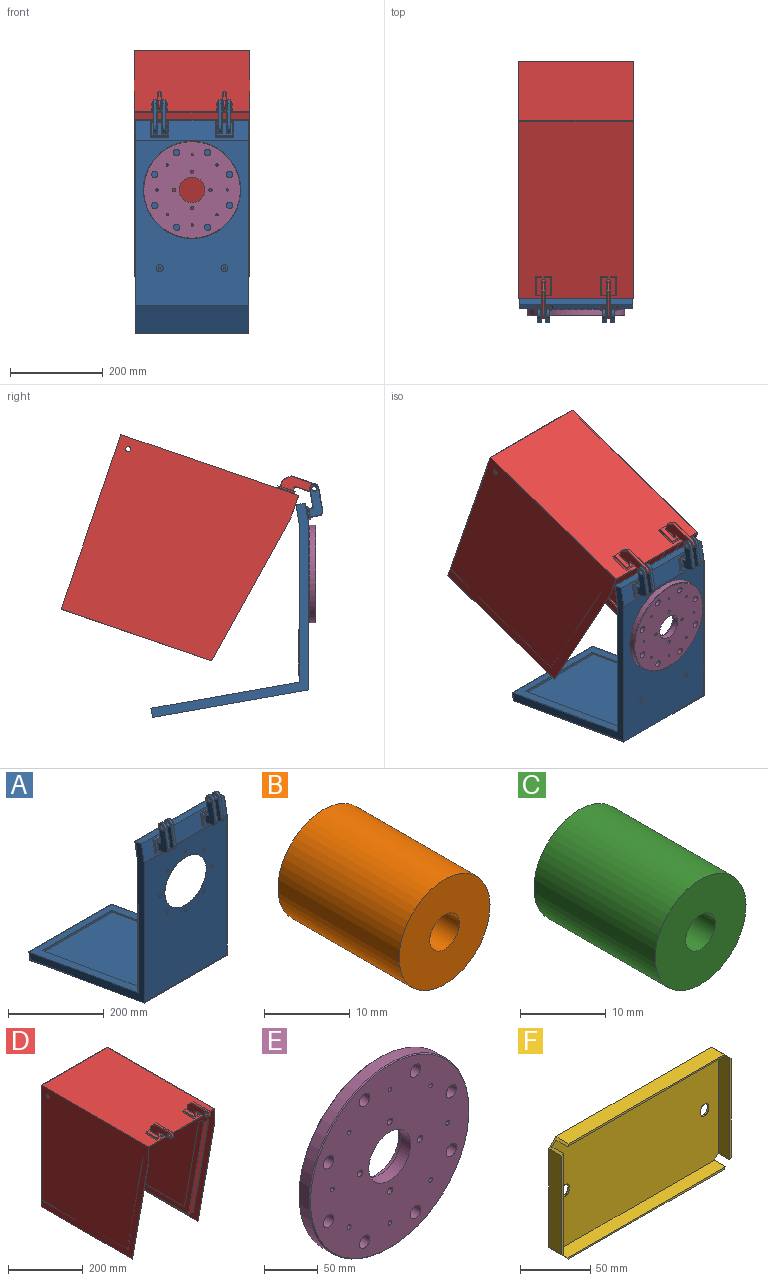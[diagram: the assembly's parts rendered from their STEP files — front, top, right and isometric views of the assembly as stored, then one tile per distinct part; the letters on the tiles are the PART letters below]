
ASSEMBLY  parts=6 mates=5
PART A: 190 faces, bbox 245x370.8x503.5 mm
  f0: plane 36x29.54mm, normal (0,-0.98,0.17), area 656mm2, adj f3,f65,f66,f67,f146,f149,f150,f153
  f1: plane 18.71x6mm, normal (0,-0.17,-0.98), area 114mm2, adj f10,f171,f172,f173
  f2: plane 18.71x6mm, normal (0,-0.17,-0.98), area 114mm2, adj f11,f144,f148,f149
  f3: plane 30.07x8.16mm, normal (1,0,0), area 90mm2, adj f0,f65,f66,f69
  f4: plane 36.44x6.43mm, normal (0,0.98,-0.17), area 222mm2, adj f6,f14,f170,f174
  f5: plane 36.44x6.43mm, normal (0,0.98,-0.17), area 222mm2, adj f7,f15,f145,f160
  f6: cylinder r=10mm len=19.85mm, axis (1,0,0), area 188.5mm2, adj f4,f8,f166,f169
  f7: cylinder r=10mm len=19.85mm, axis (1,0,0), area 188.5mm2, adj f5,f9,f143,f158
  f8: plane 49.24x8.68mm, normal (0,-0.98,0.17), area 300mm2, adj f6,f10,f164,f165
  f9: plane 49.24x8.68mm, normal (0,-0.98,0.17), area 300mm2, adj f7,f11,f141,f155
  f10: cylinder r=10mm len=11.58mm, axis (1,0,0), area 94.2mm2, adj f1,f8,f167,f168
  f11: cylinder r=10mm len=11.58mm, axis (1,0,0), area 94.2mm2, adj f2,f9,f142,f152
  f12: plane 6x5.91mm, normal (0,0.17,0.98), area 36mm2, adj f14,f179,f182,f185
  f13: plane 6x5.91mm, normal (0,0.17,0.98), area 36mm2, adj f15,f151,f157,f161
  f14: cylinder r=3mm len=6mm, axis (1,0,0), area 28.3mm2, adj f4,f12,f175,f178
  f15: cylinder r=3mm len=6mm, axis (1,0,0), area 28.3mm2, adj f5,f13,f147,f162
  f16: cylinder r=5mm len=10mm, axis (1,0,0), area 188.5mm2, adj f186,f187
  f17: plane 36x29.54mm, normal (0,-0.98,0.17), area 656mm2, adj f61,f62,f63,f64,f94,f98,f99,f102
  f18: plane 18.71x6mm, normal (0,-0.17,-0.98), area 114mm2, adj f82,f113,f118,f119
  f19: plane 49.24x8.68mm, normal (0,-0.98,0.17), area 300mm2, adj f20,f24,f88,f96
  f20: cylinder r=10mm len=19.85mm, axis (1,0,0), area 188.5mm2, adj f19,f21,f90,f101
  f21: plane 36.44x6.43mm, normal (0,0.98,-0.17), area 222mm2, adj f20,f22,f92,f104
  f22: cylinder r=3mm len=6mm, axis (1,0,0), area 28.3mm2, adj f21,f23,f95,f107
  f23: plane 6x5.91mm, normal (0,0.17,0.98), area 36mm2, adj f22,f100,f106,f109
  f24: cylinder r=10mm len=11.58mm, axis (1,0,0), area 94.2mm2, adj f19,f81,f89,f93
  f25: cylinder r=5mm len=10mm, axis (1,0,0), area 188.5mm2, adj f132,f134
  f26: plane 245x45.3mm, normal (0,-0.98,0.17), area 8550mm2, adj f34,f38,f39,f40,f68,f69,f70,f71
  f27: plane 339.86x18.5mm, normal (0,-1,0), area 6287.4mm2, adj f29,f45,f56,f57
  f28: plane 245x43.58mm, normal (0,0.98,-0.17), area 5870mm2, adj f30,f37,f38,f39,f40,f57,f59,f60
  f29: plane 320.04x242mm, normal (0,-0.17,-0.98), area 15816.6mm2, adj f27,f31,f44,f45,f46,f57,f58,f59
  f30: plane 338.47x20mm, normal (0,1,0), area 6769.4mm2, adj f28,f33,f40,f59
  f31: plane 339.86x18.5mm, normal (0,-1,0), area 6287.4mm2, adj f29,f46,f56,f59
  f32: plane 242x16.74mm, normal (0,-0.17,-0.98), area 4114mm2, adj f41,f45,f46,f56
  f33: plane 320.28x245mm, normal (0,0.17,0.98), area 17108.7mm2, adj f30,f36,f37,f39,f40,f57,f58,f59
  f34: plane 357x245mm, normal (0,-1,0), area 75428.9mm2, adj f26,f35,f39,f40,f47,f48,f49,f50
  f35: plane 336.8x245mm, normal (0,-0.17,-0.98), area 83790mm2, adj f34,f36,f39,f40
  f36: plane 245x19.7mm, normal (0,0.98,-0.17), area 4900mm2, adj f33,f35,f39,f40
  f37: plane 338.47x20mm, normal (0,1,0), area 6769.4mm2, adj f28,f33,f39,f57
  f38: plane 245x19.7mm, normal (0,0.17,0.98), area 4900mm2, adj f26,f28,f39,f40
  f39: plane 461.69x340.28mm, normal (1,0,0), area 14529.4mm2, adj f26,f28,f33,f34,f35,f36,f37,f38
  f40: plane 461.69x340.28mm, normal (-1,0,0), area 14529.4mm2, adj f26,f28,f30,f33,f34,f35,f36,f38
  f41: plane 242x43.69mm, normal (0,0.98,-0.17), area 10737.2mm2, adj f32,f42,f45,f46
  f42: plane 355.61x242mm, normal (0,1,0), area 73634.5mm2, adj f41,f43,f45,f46,f47,f48,f49,f50
  f43: plane 334.09x242mm, normal (0,0.17,0.98), area 82096.4mm2, adj f42,f44,f45,f46
  f44: plane 242x16.74mm, normal (0,-0.98,0.17), area 4114mm2, adj f29,f43,f45,f46
  f45: plane 458.21x337.04mm, normal (-1,0,0), area 12299mm2, adj f27,f29,f32,f41,f42,f43,f44,f56
  f46: plane 458.21x337.04mm, normal (1,0,0), area 12299mm2, adj f29,f31,f32,f41,f42,f43,f44,f56
  f47: cylinder r=3.5mm len=7mm, axis (0,-1,0), area 33mm2, adj f34,f42
  f48: cylinder r=3.5mm len=7mm, axis (0,-1,0), area 33mm2, adj f34,f42
  f49: cylinder r=3.5mm len=7mm, axis (0,-1,0), area 33mm2, adj f34,f42
  f50: cylinder r=3.5mm len=7mm, axis (0,-1,0), area 33mm2, adj f34,f42
  f51: cylinder r=3.5mm len=7mm, axis (0,-1,0), area 33mm2, adj f34,f42
  f52: cylinder r=61.1mm len=122.2mm, axis (0,-1,0), area 192mm2, adj f34,f189
  f53: cylinder r=3.5mm len=7mm, axis (0,-1,0), area 33mm2, adj f34,f42
  f54: cylinder r=3.5mm len=7mm, axis (0,-1,0), area 33mm2, adj f34,f42
  f55: cylinder r=3.5mm len=7mm, axis (0,-1,0), area 33mm2, adj f34,f42
  f56: plane 242x42.23mm, normal (0,-0.98,0.17), area 5379.1mm2, adj f27,f31,f32,f45,f46,f57,f59,f60
  f57: plane 417.09x302.08mm, normal (-1,0,0), area 1004mm2, adj f27,f28,f29,f33,f37,f56,f58,f60
  f58: plane 205x1.48mm, normal (0,-0.98,0.17), area 307.5mm2, adj f29,f33,f57,f59
  f59: plane 417.09x302.08mm, normal (1,0,0), area 1004mm2, adj f28,f29,f30,f31,f33,f56,f58,f60
  f60: plane 205x1.48mm, normal (0,-0.17,-0.98), area 307.5mm2, adj f28,f56,f57,f59
  f61: plane 30.07x8.16mm, normal (-1,0,0), area 90mm2, adj f17,f62,f64,f72
  f62: plane 36x2.95mm, normal (0,-0.17,-0.98), area 108mm2, adj f17,f61,f63,f74
  f63: plane 30.07x8.16mm, normal (1,0,0), area 90mm2, adj f17,f62,f64,f75
  f64: plane 36x2.95mm, normal (0,0.17,0.98), area 108mm2, adj f17,f61,f63,f73
  f65: plane 36x2.95mm, normal (0,-0.17,-0.98), area 108mm2, adj f0,f3,f67,f68
  f66: plane 36x2.95mm, normal (0,0.17,0.98), area 108mm2, adj f0,f3,f67,f71
  f67: plane 30.07x8.16mm, normal (-1,0,0), area 90mm2, adj f0,f65,f66,f70
  f68: plane 40x2.32mm, normal (0,-0.82,-0.57), area 107.5mm2, adj f26,f65,f69,f70
  f69: plane 33.48x7.53mm, normal (0.71,-0.7,0.12), area 90.5mm2, adj f3,f26,f68,f71
  f70: plane 33.48x7.53mm, normal (-0.71,-0.7,0.12), area 90.5mm2, adj f26,f67,f68,f71
  f71: plane 40x2.32mm, normal (0,-0.57,0.82), area 107.5mm2, adj f26,f66,f69,f70
  f72: plane 33.48x7.53mm, normal (-0.71,-0.7,0.12), area 90.5mm2, adj f26,f61,f73,f74
  f73: plane 40x2.32mm, normal (0,-0.57,0.82), area 107.5mm2, adj f26,f64,f72,f75
  f74: plane 40x2.32mm, normal (0,-0.82,-0.57), area 107.5mm2, adj f26,f62,f72,f75
  f75: plane 33.48x7.53mm, normal (0.71,-0.7,0.12), area 90.5mm2, adj f26,f63,f73,f74
  f76: plane 49.24x8.68mm, normal (0,-0.98,0.17), area 300mm2, adj f77,f82,f110,f122
  f77: cylinder r=10mm len=19.85mm, axis (1,0,0), area 188.5mm2, adj f76,f78,f112,f125
  f78: plane 36.44x6.43mm, normal (0,0.98,-0.17), area 222mm2, adj f77,f79,f114,f128
  f79: cylinder r=3mm len=6mm, axis (1,0,0), area 28.3mm2, adj f78,f80,f116,f130
  f80: plane 6x5.91mm, normal (0,0.17,0.98), area 36mm2, adj f79,f121,f127,f131
  f81: plane 18.71x6mm, normal (0,-0.17,-0.98), area 114mm2, adj f24,f91,f97,f98
  f82: cylinder r=10mm len=11.58mm, axis (1,0,0), area 94.2mm2, adj f18,f76,f111,f117
  f83: cylinder r=5mm len=10mm, axis (1,0,0), area 188.5mm2, adj f133,f135
  f84: plane 70.4x29.27mm, normal (-1,0,0), area 1242.2mm2, adj f93,f96,f97,f101,f104,f105,f107,f109
  f85: plane 70.4x29.27mm, normal (1,0,0), area 1242.2mm2, adj f110,f111,f112,f113,f114,f116,f120,f121
  f86: plane 70.4x29.27mm, normal (1,0,0), area 1242.2mm2, adj f88,f89,f90,f91,f92,f95,f99,f100
  f87: plane 70.4x29.27mm, normal (-1,0,0), area 1242.2mm2, adj f117,f118,f122,f125,f126,f128,f130,f131
  f88: plane 49.41x9.67mm, normal (0.71,-0.7,0.12), area 70.7mm2, adj f19,f86,f89,f90
  f89: cone r=9mm half-angle=45deg, axis (-1,0,0), area 21.1mm2, adj f24,f86,f88,f91
  f90: cone r=9mm half-angle=45deg, axis (-1,0,0), area 42.2mm2, adj f20,f86,f88,f92
  f91: plane 18.89x4.28mm, normal (0.71,-0.12,-0.7), area 26.9mm2, adj f81,f86,f89,f94
  f92: plane 36.61x7.41mm, normal (0.71,0.7,-0.12), area 52.3mm2, adj f21,f86,f90,f95
  f93: cone r=9mm half-angle=45deg, axis (1,0,0), area 21.1mm2, adj f24,f84,f96,f97
  f94: plane 2.14x2mm, normal (0.58,-0.67,-0.47), area 2.6mm2, adj f17,f91,f98,f99
  f95: cone r=3mm half-angle=45deg, axis (1,0,0), area 7.8mm2, adj f22,f86,f92,f100
  f96: plane 49.41x9.67mm, normal (-0.71,-0.7,0.12), area 70.7mm2, adj f19,f84,f93,f101
  f97: plane 18.89x4.28mm, normal (-0.71,-0.12,-0.7), area 26.9mm2, adj f81,f84,f93,f102
  f98: plane 6x1.16mm, normal (0,-0.82,-0.57), area 8.5mm2, adj f17,f81,f94,f102
  f99: plane 17.9x4.11mm, normal (0.71,-0.7,0.12), area 25.5mm2, adj f17,f86,f94,f103
  f100: plane 6.08x2.03mm, normal (0.71,0.12,0.7), area 8.5mm2, adj f23,f86,f95,f103
  f101: cone r=9mm half-angle=45deg, axis (1,0,0), area 42.2mm2, adj f20,f84,f96,f104
  f102: plane 2.14x2mm, normal (-0.58,-0.67,-0.47), area 2.6mm2, adj f17,f97,f98,f105
  f103: plane 2x1.97mm, normal (0.58,-0.47,0.67), area 2.6mm2, adj f17,f99,f100,f106
  f104: plane 36.61x7.41mm, normal (-0.71,0.7,-0.12), area 52.3mm2, adj f21,f84,f101,f107
  f105: plane 17.9x4.11mm, normal (-0.71,-0.7,0.12), area 25.5mm2, adj f17,f84,f102,f108
  f106: plane 6x1.16mm, normal (0,-0.57,0.82), area 8.5mm2, adj f17,f23,f103,f108
  f107: cone r=3mm half-angle=45deg, axis (-1,0,0), area 7.8mm2, adj f22,f84,f104,f109
  f108: plane 2x1.97mm, normal (-0.58,-0.47,0.67), area 2.6mm2, adj f17,f105,f106,f109
  f109: plane 6.08x2.03mm, normal (-0.71,0.12,0.7), area 8.5mm2, adj f23,f84,f107,f108
  f110: plane 49.41x9.67mm, normal (0.71,-0.7,0.12), area 70.7mm2, adj f76,f85,f111,f112
  f111: cone r=10mm half-angle=45deg, axis (-1,0,0), area 21.1mm2, adj f82,f85,f110,f113
  f112: cone r=10mm half-angle=45deg, axis (-1,0,0), area 42.2mm2, adj f77,f85,f110,f114
  f113: plane 18.89x4.28mm, normal (0.71,-0.12,-0.7), area 26.9mm2, adj f18,f85,f111,f115
  f114: plane 36.61x7.41mm, normal (0.71,0.7,-0.12), area 52.3mm2, adj f78,f85,f112,f116
  f115: plane 2.14x2mm, normal (0.58,-0.67,-0.47), area 2.6mm2, adj f17,f113,f119,f120
  f116: cone r=4mm half-angle=45deg, axis (1,0,0), area 7.8mm2, adj f79,f85,f114,f121
  f117: cone r=10mm half-angle=45deg, axis (1,0,0), area 21.1mm2, adj f82,f87,f118,f122
  f118: plane 18.89x4.28mm, normal (-0.71,-0.12,-0.7), area 26.9mm2, adj f18,f87,f117,f123
  f119: plane 6x1.16mm, normal (0,-0.82,-0.57), area 8.5mm2, adj f17,f18,f115,f123
  f120: plane 17.9x4.11mm, normal (0.71,-0.7,0.12), area 25.5mm2, adj f17,f85,f115,f124
  f121: plane 6.08x2.03mm, normal (0.71,0.12,0.7), area 8.5mm2, adj f80,f85,f116,f124
  f122: plane 49.41x9.67mm, normal (-0.71,-0.7,0.12), area 70.7mm2, adj f76,f87,f117,f125
  f123: plane 2.14x2mm, normal (-0.58,-0.67,-0.47), area 2.6mm2, adj f17,f118,f119,f126
  f124: plane 2x1.97mm, normal (0.58,-0.47,0.67), area 2.6mm2, adj f17,f120,f121,f127
  f125: cone r=10mm half-angle=45deg, axis (1,0,0), area 42.2mm2, adj f77,f87,f122,f128
  f126: plane 17.9x4.11mm, normal (-0.71,-0.7,0.12), area 25.5mm2, adj f17,f87,f123,f129
  f127: plane 6x1.16mm, normal (0,-0.57,0.82), area 8.5mm2, adj f17,f80,f124,f129
  f128: plane 36.61x7.41mm, normal (-0.71,0.7,-0.12), area 52.3mm2, adj f78,f87,f125,f130
  f129: plane 2x1.97mm, normal (-0.58,-0.47,0.67), area 2.6mm2, adj f17,f126,f127,f131
  f130: cone r=4mm half-angle=45deg, axis (-1,0,0), area 7.8mm2, adj f79,f87,f128,f131
  f131: plane 6.08x2.03mm, normal (-0.71,0.12,0.7), area 8.5mm2, adj f80,f87,f129,f130
  f132: cone r=5mm half-angle=45deg, axis (-1,0,0), area 48.9mm2, adj f25,f84
  f133: cone r=6mm half-angle=45deg, axis (-1,0,0), area 48.9mm2, adj f83,f87
  f134: cone r=5mm half-angle=45deg, axis (1,0,0), area 48.9mm2, adj f25,f86
  f135: cone r=6mm half-angle=45deg, axis (1,0,0), area 48.9mm2, adj f83,f85
  f136: plane 70.4x29.27mm, normal (-1,0,0), area 1242.2mm2, adj f164,f166,f167,f170,f171,f175,f179,f180
  f137: plane 70.4x29.27mm, normal (1,0,0), area 1242.2mm2, adj f141,f142,f143,f144,f145,f147,f150,f151
  f138: plane 70.4x29.27mm, normal (1,0,0), area 1242.2mm2, adj f165,f168,f169,f173,f174,f178,f181,f182
  f139: plane 70.4x29.27mm, normal (-1,0,0), area 1242.2mm2, adj f148,f152,f155,f156,f158,f160,f161,f162
  f140: cylinder r=5mm len=10mm, axis (1,0,0), area 188.5mm2, adj f163,f188
  f141: plane 49.41x9.67mm, normal (0.71,-0.7,0.12), area 70.7mm2, adj f9,f137,f142,f143
  f142: cone r=10mm half-angle=45deg, axis (-1,0,0), area 21.1mm2, adj f11,f137,f141,f144
  f143: cone r=10mm half-angle=45deg, axis (-1,0,0), area 42.2mm2, adj f7,f137,f141,f145
  f144: plane 18.89x4.28mm, normal (0.71,-0.12,-0.7), area 26.9mm2, adj f2,f137,f142,f146
  f145: plane 36.61x7.41mm, normal (0.71,0.7,-0.12), area 52.3mm2, adj f5,f137,f143,f147
  f146: plane 2.14x2mm, normal (0.58,-0.67,-0.47), area 2.6mm2, adj f0,f144,f149,f150
  f147: cone r=4mm half-angle=45deg, axis (1,0,0), area 7.8mm2, adj f15,f137,f145,f151
  f148: plane 18.89x4.28mm, normal (-0.71,-0.12,-0.7), area 26.9mm2, adj f2,f139,f152,f153
  f149: plane 6x1.16mm, normal (0,-0.82,-0.57), area 8.5mm2, adj f0,f2,f146,f153
  f150: plane 17.9x4.11mm, normal (0.71,-0.7,0.12), area 25.5mm2, adj f0,f137,f146,f154
  f151: plane 6.08x2.03mm, normal (0.71,0.12,0.7), area 8.5mm2, adj f13,f137,f147,f154
  f152: cone r=10mm half-angle=45deg, axis (1,0,0), area 21.1mm2, adj f11,f139,f148,f155
  f153: plane 2.14x2mm, normal (-0.58,-0.67,-0.47), area 2.6mm2, adj f0,f148,f149,f156
  f154: plane 2x1.97mm, normal (0.58,-0.47,0.67), area 2.6mm2, adj f0,f150,f151,f157
  f155: plane 49.41x9.67mm, normal (-0.71,-0.7,0.12), area 70.7mm2, adj f9,f139,f152,f158
  f156: plane 17.9x4.11mm, normal (-0.71,-0.7,0.12), area 25.5mm2, adj f0,f139,f153,f159
  f157: plane 6x1.16mm, normal (0,-0.57,0.82), area 8.5mm2, adj f0,f13,f154,f159
  f158: cone r=10mm half-angle=45deg, axis (1,0,0), area 42.2mm2, adj f7,f139,f155,f160
  f159: plane 2x1.97mm, normal (-0.58,-0.47,0.67), area 2.6mm2, adj f0,f156,f157,f161
  f160: plane 36.61x7.41mm, normal (-0.71,0.7,-0.12), area 52.3mm2, adj f5,f139,f158,f162
  f161: plane 6.08x2.03mm, normal (-0.71,0.12,0.7), area 8.5mm2, adj f13,f139,f159,f162
  f162: cone r=4mm half-angle=45deg, axis (-1,0,0), area 7.8mm2, adj f15,f139,f160,f161
  f163: cone r=6mm half-angle=45deg, axis (-1,0,0), area 48.9mm2, adj f139,f140
  f164: plane 49.41x9.67mm, normal (-0.71,-0.7,0.12), area 70.7mm2, adj f8,f136,f166,f167
  f165: plane 49.41x9.67mm, normal (0.71,-0.7,0.12), area 70.7mm2, adj f8,f138,f168,f169
  f166: cone r=10mm half-angle=45deg, axis (1,0,0), area 42.2mm2, adj f6,f136,f164,f170
  f167: cone r=10mm half-angle=45deg, axis (1,0,0), area 21.1mm2, adj f10,f136,f164,f171
  f168: cone r=10mm half-angle=45deg, axis (-1,0,0), area 21.1mm2, adj f10,f138,f165,f173
  f169: cone r=10mm half-angle=45deg, axis (-1,0,0), area 42.2mm2, adj f6,f138,f165,f174
  f170: plane 36.61x7.41mm, normal (-0.71,0.7,-0.12), area 52.3mm2, adj f4,f136,f166,f175
  f171: plane 18.89x4.28mm, normal (-0.71,-0.12,-0.7), area 26.9mm2, adj f1,f136,f167,f176
  f172: plane 6x1.16mm, normal (0,-0.82,-0.57), area 8.5mm2, adj f0,f1,f176,f177
  f173: plane 18.89x4.28mm, normal (0.71,-0.12,-0.7), area 26.9mm2, adj f1,f138,f168,f177
  f174: plane 36.61x7.41mm, normal (0.71,0.7,-0.12), area 52.3mm2, adj f4,f138,f169,f178
  f175: cone r=4mm half-angle=45deg, axis (-1,0,0), area 7.8mm2, adj f14,f136,f170,f179
  f176: plane 2.14x2mm, normal (-0.58,-0.67,-0.47), area 2.6mm2, adj f0,f171,f172,f180
  f177: plane 2.14x2mm, normal (0.58,-0.67,-0.47), area 2.6mm2, adj f0,f172,f173,f181
  f178: cone r=4mm half-angle=45deg, axis (1,0,0), area 7.8mm2, adj f14,f138,f174,f182
  f179: plane 6.08x2.03mm, normal (-0.71,0.12,0.7), area 8.5mm2, adj f12,f136,f175,f183
  f180: plane 17.9x4.11mm, normal (-0.71,-0.7,0.12), area 25.5mm2, adj f0,f136,f176,f183
  f181: plane 17.9x4.11mm, normal (0.71,-0.7,0.12), area 25.5mm2, adj f0,f138,f177,f184
  f182: plane 6.08x2.03mm, normal (0.71,0.12,0.7), area 8.5mm2, adj f12,f138,f178,f184
  f183: plane 2x1.97mm, normal (-0.58,-0.47,0.67), area 2.6mm2, adj f0,f179,f180,f185
  f184: plane 2x1.97mm, normal (0.58,-0.47,0.67), area 2.6mm2, adj f0,f181,f182,f185
  f185: plane 6x1.16mm, normal (0,-0.57,0.82), area 8.5mm2, adj f0,f12,f183,f184
  f186: cone r=6mm half-angle=45deg, axis (-1,0,0), area 48.9mm2, adj f16,f136
  f187: cone r=6mm half-angle=45deg, axis (1,0,0), area 48.9mm2, adj f16,f138
  f188: cone r=6mm half-angle=45deg, axis (1,0,0), area 48.9mm2, adj f137,f140
  f189: cone r=61.1mm half-angle=45deg, axis (0,1,0), area 547.4mm2, adj f42,f52
PART B: 4 faces, bbox 15x20x15 mm
  f0: cylinder r=2.46mm len=20mm, axis (0,1,0), area 309.1mm2, adj f2,f3
  f1: cylinder r=7.5mm len=20mm, axis (0,1,0), area 942.5mm2, adj f2,f3
  f2: plane 15x15mm, normal (0,-1,0), area 157.7mm2, adj f0,f1
  f3: plane 15x15mm, normal (0,1,0), area 157.7mm2, adj f0,f1
PART C: 4 faces, bbox 15x20x15 mm
  f0: cylinder r=7.5mm len=20mm, axis (0,1,0), area 942.5mm2, adj f2,f3
  f1: cylinder r=2.46mm len=20mm, axis (0,1,0), area 309.1mm2, adj f2,f3
  f2: plane 15x15mm, normal (0,-1,0), area 157.7mm2, adj f0,f1
  f3: plane 15x15mm, normal (0,1,0), area 157.7mm2, adj f0,f1
PART D: 128 faces, bbox 250x442x433 mm
  f0: plane 40x30mm, normal (0,0,1), area 888mm2, adj f68,f69,f70,f71,f104,f105,f108,f109
  f1: plane 40x30mm, normal (0,0,1), area 888mm2, adj f64,f65,f66,f67,f82,f83,f86,f87
  f2: plane 38x6mm, normal (0,0,-1), area 228mm2, adj f3,f8,f94,f95
  f3: cylinder r=10mm len=20mm, axis (-1,0,0), area 188.5mm2, adj f2,f4,f97,f98
  f4: plane 56x6mm, normal (0,0,1), area 336mm2, adj f3,f5,f101,f102
  f5: plane 15x15mm, normal (0,0.71,0.71), area 127.3mm2, adj f4,f6,f106,f107
  f6: plane 14x6mm, normal (0,1,0), area 84mm2, adj f5,f110,f111,f115
  f7: plane 6x6mm, normal (0,-1,0), area 36mm2, adj f8,f100,f103,f104
  f8: cylinder r=3mm len=6mm, axis (-1,0,0), area 28.3mm2, adj f2,f7,f96,f99
  f9: cylinder r=5mm len=10mm, axis (-1,0,0), area 188.5mm2, adj f117,f119
  f10: plane 79x28mm, normal (1,0,0), area 1453.7mm2, adj f94,f96,f97,f100,f101,f106,f109,f110
  f11: plane 79x28mm, normal (-1,0,0), area 1453.7mm2, adj f95,f98,f99,f102,f103,f107,f111,f112
  f12: plane 38x6mm, normal (0,0,-1), area 228mm2, adj f13,f18,f72,f73
  f13: cylinder r=10mm len=20mm, axis (-1,0,0), area 188.5mm2, adj f12,f14,f75,f76
  f14: plane 56x6mm, normal (0,0,1), area 336mm2, adj f13,f15,f79,f80
  f15: plane 15x15mm, normal (0,0.71,0.71), area 127.3mm2, adj f14,f16,f84,f85
  f16: plane 14x6mm, normal (0,1,0), area 84mm2, adj f15,f88,f89,f93
  f17: plane 6x6mm, normal (0,-1,0), area 36mm2, adj f18,f78,f81,f82
  f18: cylinder r=3mm len=6mm, axis (-1,0,0), area 28.3mm2, adj f12,f17,f74,f77
  f19: cylinder r=5mm len=10mm, axis (-1,0,0), area 188.5mm2, adj f116,f118
  f20: plane 79x28mm, normal (1,0,0), area 1453.7mm2, adj f72,f74,f75,f78,f79,f84,f87,f88
  f21: plane 79x28mm, normal (-1,0,0), area 1453.7mm2, adj f73,f76,f77,f80,f81,f85,f89,f90
  f22: plane 18x3.94mm, normal (0,-0.17,0.98), area 29.7mm2, adj f34,f51,f57,f58,f60,f61,f62
  f23: plane 343.5x250mm, normal (0,0,-1), area 1401mm2, adj f24,f27,f28,f29,f30,f32,f33,f34
  f24: plane 348.78x61.5mm, normal (0,-0.98,-0.17), area 531.2mm2, adj f23,f25,f30,f34
  f25: plane 250x49.22mm, normal (0,-1,0), area 518.1mm2, adj f24,f26,f27,f29,f30,f31,f33,f34
  f26: plane 405x250mm, normal (0,0,1), area 98258mm2, adj f25,f28,f29,f30,f120,f121,f122,f123
  f27: plane 348.78x61.5mm, normal (0,-0.98,-0.17), area 531.2mm2, adj f23,f25,f29,f33
  f28: plane 398x250mm, normal (0,1,0), area 99500mm2, adj f23,f26,f29,f30
  f29: plane 405x398mm, normal (1,0,0), area 150369.9mm2, adj f23,f25,f26,f27,f28,f36
  f30: plane 405x398mm, normal (-1,0,0), area 150369.9mm2, adj f23,f24,f25,f26,f28,f35
  f31: plane 403.5x247mm, normal (0,0,-1), area 99664.5mm2, adj f25,f32,f33,f34
  f32: plane 396.5x247mm, normal (0,-1,0), area 97935.5mm2, adj f23,f31,f33,f34
  f33: plane 403.5x396.5mm, normal (-1,0,0), area 147520.5mm2, adj f23,f25,f27,f31,f32,f36,f39,f44
  f34: plane 403.5x396.5mm, normal (1,0,0), area 147521.2mm2, adj f22,f23,f24,f25,f31,f32,f35,f55
  f35: cylinder r=5.5mm len=11mm, axis (1,0,0), area 51.8mm2, adj f30,f34
  f36: cylinder r=5.5mm len=11mm, axis (1,0,0), area 51.8mm2, adj f29,f33
  f37: plane 331.88x58.52mm, normal (0,-0.98,-0.17), area 5729mm2, adj f38,f44,f45,f49
  f38: plane 322.27x17mm, normal (0,0,-1), area 5478.7mm2, adj f37,f39,f45,f50
  f39: plane 18x4mm, normal (0,1,0), area 29.8mm2, adj f33,f38,f40,f45,f47,f48,f50
  f40: cylinder r=15mm len=15mm, axis (1,0,0), area 35.3mm2, adj f39,f41,f45,f48
  f41: plane 292.17x1.5mm, normal (0,0,1), area 438.3mm2, adj f40,f42,f45,f48
  f42: plane 302.23x53.29mm, normal (0,0.98,0.17), area 460.3mm2, adj f41,f43,f45,f48
  f43: cylinder r=15mm len=17.38mm, axis (1,0,0), area 35.3mm2, adj f42,f44,f45,f48
  f44: plane 18x3.94mm, normal (0,-0.17,0.98), area 29.7mm2, adj f33,f37,f43,f45,f46,f48,f49
  f45: plane 380.79x332.63mm, normal (-1,0,0), area 11498.5mm2, adj f37,f38,f39,f40,f41,f42,f43,f44
  f46: plane 330.64x58.3mm, normal (0,0.98,0.17), area 5539.7mm2, adj f33,f44,f47,f48
  f47: plane 321.02x16.5mm, normal (0,0,1), area 5296.8mm2, adj f33,f39,f46,f48
  f48: plane 379.32x331.13mm, normal (1,0,0), area 10511.5mm2, adj f39,f40,f41,f42,f43,f44,f46,f47
  f49: plane 332.88x59.5mm, normal (-0.71,-0.7,-0.12), area 477.2mm2, adj f33,f37,f44,f50
  f50: plane 323.11x1mm, normal (-0.71,0,-0.71), area 456.4mm2, adj f33,f38,f39,f49
  f51: cylinder r=15mm len=17.38mm, axis (-1,0,0), area 35.3mm2, adj f22,f52,f58,f61
  f52: plane 302.23x53.29mm, normal (0,0.98,0.17), area 460.3mm2, adj f51,f53,f58,f61
  f53: plane 291.9x1.5mm, normal (0,0,1), area 437.8mm2, adj f52,f54,f58,f61
  f54: cylinder r=15mm len=15mm, axis (-1,0,0), area 35.3mm2, adj f53,f55,f58,f61
  f55: plane 18x4mm, normal (0,1,0), area 29.8mm2, adj f34,f54,f56,f58,f59,f61,f63
  f56: plane 322x17mm, normal (0,0,-1), area 5474mm2, adj f55,f57,f58,f63
  f57: plane 331.88x58.52mm, normal (0,-0.98,-0.17), area 5729mm2, adj f22,f56,f58,f62
  f58: plane 380.52x332.63mm, normal (1,0,0), area 11493.6mm2, adj f22,f51,f52,f53,f54,f55,f56,f57
  f59: plane 320.74x16.5mm, normal (0,0,1), area 5292.2mm2, adj f34,f55,f60,f61
  f60: plane 330.64x58.3mm, normal (0,0.98,0.17), area 5539.7mm2, adj f22,f34,f59,f61
  f61: plane 379.04x331.13mm, normal (-1,0,0), area 10506.9mm2, adj f22,f51,f52,f53,f54,f55,f59,f60
  f62: plane 332.88x59.5mm, normal (0.71,-0.7,-0.12), area 477.2mm2, adj f22,f34,f57,f63
  f63: plane 322.84x1mm, normal (0.71,0,-0.71), area 456mm2, adj f34,f55,f56,f62
  f64: plane 40x3mm, normal (1,0,0), area 120mm2, adj f1,f65,f67,f124
  f65: plane 30x3mm, normal (0,1,0), area 90mm2, adj f1,f64,f66,f125
  f66: plane 40x3mm, normal (-1,0,0), area 120mm2, adj f1,f65,f67,f127
  f67: plane 30x3mm, normal (0,-1,0), area 90mm2, adj f1,f64,f66,f126
  f68: plane 40x3mm, normal (1,0,0), area 120mm2, adj f0,f69,f71,f121
  f69: plane 30x3mm, normal (0,1,0), area 90mm2, adj f0,f68,f70,f123
  f70: plane 40x3mm, normal (-1,0,0), area 120mm2, adj f0,f69,f71,f122
  f71: plane 30x3mm, normal (0,-1,0), area 90mm2, adj f0,f68,f70,f120
  f72: plane 38x1mm, normal (0.71,0,-0.71), area 53.7mm2, adj f12,f20,f74,f75
  f73: plane 38x1mm, normal (-0.71,0,-0.71), area 53.7mm2, adj f12,f21,f76,f77
  f74: cone r=4mm half-angle=45deg, axis (1,0,0), area 7.8mm2, adj f18,f20,f72,f78
  f75: cone r=10mm half-angle=45deg, axis (-1,0,0), area 42.2mm2, adj f13,f20,f72,f79
  f76: cone r=9mm half-angle=45deg, axis (1,0,0), area 42.2mm2, adj f13,f21,f73,f80
  f77: cone r=3mm half-angle=45deg, axis (-1,0,0), area 7.8mm2, adj f18,f21,f73,f81
  f78: plane 6x1mm, normal (0.71,-0.71,0), area 8.5mm2, adj f17,f20,f74,f83
  f79: plane 56x1mm, normal (0.71,0,0.71), area 78.9mm2, adj f14,f20,f75,f84
  f80: plane 56x1mm, normal (-0.71,0,0.71), area 78.9mm2, adj f14,f21,f76,f85
  f81: plane 6x1mm, normal (-0.71,-0.71,0), area 8.5mm2, adj f17,f21,f77,f86
  f82: plane 6x1mm, normal (0,-0.71,0.71), area 8.5mm2, adj f1,f17,f83,f86
  f83: plane 2x2mm, normal (0.58,-0.58,0.58), area 2.6mm2, adj f1,f78,f82,f87
  f84: plane 15.41x15.41mm, normal (0.71,0.5,0.5), area 29.4mm2, adj f15,f20,f79,f88
  f85: plane 15.41x15.41mm, normal (-0.71,0.5,0.5), area 29.4mm2, adj f15,f21,f80,f89
  f86: plane 2x2mm, normal (-0.58,-0.58,0.58), area 2.6mm2, adj f1,f81,f82,f90
  f87: plane 28x1mm, normal (0.71,0,0.71), area 39.6mm2, adj f1,f20,f83,f91
  f88: plane 14x1mm, normal (0.71,0.71,0), area 19.5mm2, adj f16,f20,f84,f91
  f89: plane 14x1mm, normal (-0.71,0.71,0), area 19.5mm2, adj f16,f21,f85,f92
  f90: plane 28x1mm, normal (-0.71,0,0.71), area 39.6mm2, adj f1,f21,f86,f92
  f91: plane 2x2mm, normal (0.58,0.58,0.58), area 2.6mm2, adj f1,f87,f88,f93
  f92: plane 2x2mm, normal (-0.58,0.58,0.58), area 2.6mm2, adj f1,f89,f90,f93
  f93: plane 6x1mm, normal (0,0.71,0.71), area 8.5mm2, adj f1,f16,f91,f92
  f94: plane 38x1mm, normal (0.71,0,-0.71), area 53.7mm2, adj f2,f10,f96,f97
  f95: plane 38x1mm, normal (-0.71,0,-0.71), area 53.7mm2, adj f2,f11,f98,f99
  f96: cone r=4mm half-angle=45deg, axis (1,0,0), area 7.8mm2, adj f8,f10,f94,f100
  f97: cone r=10mm half-angle=45deg, axis (-1,0,0), area 42.2mm2, adj f3,f10,f94,f101
  f98: cone r=9mm half-angle=45deg, axis (1,0,0), area 42.2mm2, adj f3,f11,f95,f102
  f99: cone r=3mm half-angle=45deg, axis (-1,0,0), area 7.8mm2, adj f8,f11,f95,f103
  f100: plane 6x1mm, normal (0.71,-0.71,0), area 8.5mm2, adj f7,f10,f96,f105
  f101: plane 56x1mm, normal (0.71,0,0.71), area 78.9mm2, adj f4,f10,f97,f106
  f102: plane 56x1mm, normal (-0.71,0,0.71), area 78.9mm2, adj f4,f11,f98,f107
  f103: plane 6x1mm, normal (-0.71,-0.71,0), area 8.5mm2, adj f7,f11,f99,f108
  f104: plane 6x1mm, normal (0,-0.71,0.71), area 8.5mm2, adj f0,f7,f105,f108
  f105: plane 2x2mm, normal (0.58,-0.58,0.58), area 2.6mm2, adj f0,f100,f104,f109
  f106: plane 15.41x15.41mm, normal (0.71,0.5,0.5), area 29.4mm2, adj f5,f10,f101,f110
  f107: plane 15.41x15.41mm, normal (-0.71,0.5,0.5), area 29.4mm2, adj f5,f11,f102,f111
  f108: plane 2x2mm, normal (-0.58,-0.58,0.58), area 2.6mm2, adj f0,f103,f104,f112
  f109: plane 28x1mm, normal (0.71,0,0.71), area 39.6mm2, adj f0,f10,f105,f113
  f110: plane 14x1mm, normal (0.71,0.71,0), area 19.5mm2, adj f6,f10,f106,f113
  f111: plane 14x1mm, normal (-0.71,0.71,0), area 19.5mm2, adj f6,f11,f107,f114
  f112: plane 28x1mm, normal (-0.71,0,0.71), area 39.6mm2, adj f0,f11,f108,f114
  f113: plane 2x2mm, normal (0.58,0.58,0.58), area 2.6mm2, adj f0,f109,f110,f115
  f114: plane 2x2mm, normal (-0.58,0.58,0.58), area 2.6mm2, adj f0,f111,f112,f115
  f115: plane 6x1mm, normal (0,0.71,0.71), area 8.5mm2, adj f0,f6,f113,f114
  f116: cone r=5mm half-angle=45deg, axis (-1,0,0), area 48.9mm2, adj f19,f21
  f117: cone r=6mm half-angle=45deg, axis (1,0,0), area 48.9mm2, adj f9,f10
  f118: cone r=6mm half-angle=45deg, axis (1,0,0), area 48.9mm2, adj f19,f20
  f119: cone r=5mm half-angle=45deg, axis (-1,0,0), area 48.9mm2, adj f9,f11
  f120: plane 34x2mm, normal (0,-0.71,0.71), area 90.5mm2, adj f26,f71,f121,f122
  f121: plane 44x2mm, normal (0.71,0,0.71), area 118.8mm2, adj f26,f68,f120,f123
  f122: plane 44x2mm, normal (-0.71,0,0.71), area 118.8mm2, adj f26,f70,f120,f123
  f123: plane 34x2mm, normal (0,0.71,0.71), area 90.5mm2, adj f26,f69,f121,f122
  f124: plane 44x2mm, normal (0.71,0,0.71), area 118.8mm2, adj f26,f64,f125,f126
  f125: plane 34x2mm, normal (0,0.71,0.71), area 90.5mm2, adj f26,f65,f124,f127
  f126: plane 34x2mm, normal (0,-0.71,0.71), area 90.5mm2, adj f26,f67,f124,f127
  f127: plane 44x2mm, normal (-0.71,0,0.71), area 118.8mm2, adj f26,f66,f125,f126
PART E: 30 faces, bbox 210x18x210 mm
  f0: cylinder r=3.5mm len=18mm, axis (0,-1,0), area 395.8mm2, adj f22,f25
  f1: cylinder r=3.5mm len=18mm, axis (0,-1,0), area 395.8mm2, adj f22,f25
  f2: cylinder r=3.5mm len=18mm, axis (0,-1,0), area 395.8mm2, adj f22,f25
  f3: cylinder r=105mm len=210mm, axis (0,-1,0), area 8576.5mm2, adj f28,f29
  f4: cylinder r=2.46mm len=15mm, axis (0,-1,0), area 231.8mm2, adj f21,f22
  f5: cylinder r=6.92mm len=15mm, axis (0,-1,0), area 651.7mm2, adj f21,f22
  f6: cylinder r=2.46mm len=15mm, axis (0,-1,0), area 231.8mm2, adj f21,f22
  f7: cylinder r=2.46mm len=15mm, axis (0,-1,0), area 231.8mm2, adj f21,f22
  f8: cylinder r=2.46mm len=15mm, axis (0,-1,0), area 231.8mm2, adj f21,f22
  f9: cylinder r=2.46mm len=15mm, axis (0,-1,0), area 231.8mm2, adj f21,f22
  f10: cylinder r=2.46mm len=15mm, axis (0,-1,0), area 231.8mm2, adj f21,f22
  f11: cylinder r=2.46mm len=15mm, axis (0,-1,0), area 231.8mm2, adj f21,f22
  f12: cylinder r=2.46mm len=15mm, axis (0,-1,0), area 231.8mm2, adj f21,f22
  f13: cylinder r=6.92mm len=15mm, axis (0,-1,0), area 651.7mm2, adj f21,f22
  f14: cylinder r=6.92mm len=15mm, axis (0,-1,0), area 651.7mm2, adj f21,f22
  f15: cylinder r=6.92mm len=15mm, axis (0,-1,0), area 651.7mm2, adj f21,f22
  f16: cylinder r=6.92mm len=15mm, axis (0,-1,0), area 651.7mm2, adj f21,f22
  f17: cylinder r=6.92mm len=15mm, axis (0,-1,0), area 651.7mm2, adj f21,f22
  f18: cylinder r=6.92mm len=15mm, axis (0,-1,0), area 651.7mm2, adj f21,f22
  f19: cylinder r=6.92mm len=15mm, axis (0,-1,0), area 651.7mm2, adj f21,f22
  f20: cylinder r=3.5mm len=18mm, axis (0,-1,0), area 395.8mm2, adj f22,f25
  f21: plane 208x208mm, normal (0,1,0), area 20935.7mm2, adj f4,f5,f6,f7,f8,f9,f10,f11
  f22: plane 208x208mm, normal (0,-1,0), area 30095.8mm2, adj f0,f1,f2,f4,f5,f6,f7,f8
  f23: cylinder r=30mm len=60mm, axis (0,-1,0), area 942.5mm2, adj f25,f27
  f24: cylinder r=61mm len=122mm, axis (0,-1,0), area 1149.8mm2, adj f21,f25
  f25: plane 122x122mm, normal (0,1,0), area 8708.5mm2, adj f0,f1,f2,f20,f23,f24
  f26: cylinder r=27.5mm len=55mm, axis (0,-1,0), area 2246.2mm2, adj f22,f27
  f27: plane 60x60mm, normal (0,1,0), area 451.6mm2, adj f23,f26
  f28: cone r=104mm half-angle=45deg, axis (0,1,0), area 928.6mm2, adj f3,f22
  f29: cone r=105mm half-angle=45deg, axis (0,-1,0), area 928.6mm2, adj f3,f21
PART F: 26 faces, bbox 170x13x100 mm
  f0: plane 13x7mm, normal (0.71,0,-0.71), area 63.6mm2, adj f5,f12,f17,f19,f20,f21,f22,f23
  f1: plane 13x7mm, normal (-0.71,0,-0.71), area 63.6mm2, adj f4,f12,f13,f19,f20,f21,f23,f24
  f2: plane 13x7mm, normal (0.71,0,0.71), area 63.6mm2, adj f3,f5,f15,f17,f19,f21,f22,f25
  f3: plane 159x1.5mm, normal (0,-1,0), area 236.3mm2, adj f2,f14,f15,f25
  f4: plane 89x1.5mm, normal (0,-1,0), area 131.3mm2, adj f1,f13,f14,f24
  f5: plane 89x1.5mm, normal (0,-1,0), area 131.3mm2, adj f0,f2,f17,f22
  f6: cylinder r=4mm len=8mm, axis (0,-1,0), area 18.8mm2, adj f7,f18,f19,f21
  f7: plane 2x1.5mm, normal (1,0,0), area 3mm2, adj f6,f8,f19,f21
  f8: cylinder r=4mm len=8mm, axis (0,-1,0), area 18.8mm2, adj f7,f18,f19,f21
  f9: plane 2x1.5mm, normal (-1,0,0), area 3mm2, adj f10,f16,f19,f21
  f10: cylinder r=4mm len=8mm, axis (0,-1,0), area 18.8mm2, adj f9,f11,f19,f21
  f11: plane 2x1.5mm, normal (1,0,0), area 3mm2, adj f10,f16,f19,f21
  f12: plane 156x13mm, normal (0,0,-1), area 2028mm2, adj f0,f1,f19,f20
  f13: plane 86x13mm, normal (-1,0,0), area 1118mm2, adj f1,f4,f14,f19
  f14: plane 13x7mm, normal (-0.71,0,0.71), area 63.6mm2, adj f3,f4,f13,f15,f19,f21,f24,f25
  f15: plane 156x13mm, normal (0,0,1), area 2028mm2, adj f2,f3,f14,f19
  f16: cylinder r=4mm len=8mm, axis (0,-1,0), area 18.8mm2, adj f9,f11,f19,f21
  f17: plane 86x13mm, normal (1,0,0), area 1118mm2, adj f0,f2,f5,f19
  f18: plane 2x1.5mm, normal (-1,0,0), area 3mm2, adj f6,f8,f19,f21
  f19: plane 170x100mm, normal (0,1,0), area 16769.5mm2, adj f0,f1,f2,f6,f7,f8,f9,f10
  f20: plane 159x1.5mm, normal (0,-1,0), area 236.3mm2, adj f0,f1,f12,f23
  f21: plane 167x97mm, normal (0,-1,0), area 16034.5mm2, adj f0,f1,f2,f6,f7,f8,f9,f10
  f22: plane 89x11.5mm, normal (-1,0,0), area 1023.5mm2, adj f0,f2,f5,f21
  f23: plane 159x11.5mm, normal (0,0,1), area 1828.5mm2, adj f0,f1,f20,f21
  f24: plane 89x11.5mm, normal (1,0,0), area 1023.5mm2, adj f1,f4,f14,f21
  f25: plane 159x11.5mm, normal (0,0,-1), area 1828.5mm2, adj f2,f3,f14,f21
PLACE A t=(-83.39,-424.75,140.29)mm fixed
PLACE B t=(-83.19,-424.75,136.38)mm
PLACE C t=(-83.39,-424.75,136.38)mm
PLACE D rot(axis=(1,0,0),18.9deg) t=(-83.39,-367.38,22.95)mm
PLACE E t=(-83.03,-424.75,140.29)mm
PLACE F t=(-83.29,-436.25,136.38)mm
MATE fastened C.f0 <-> A.f42  axis (0,-1,0) through (-13.39,-408.25,-28.62)mm
MATE fastened F.f8 <-> C.f3  axis (0,-1,0) through (-13.39,-388.25,-29.62)mm
MATE revolute D.f13 <-> A.f143  axis (-1,0,0) through (-10.39,-421.53,324.43)mm
MATE fastened F.f16 <-> B.f3  axis (0,-1,0) through (-153.19,-388.25,-29.62)mm
MATE fastened E.f21 <-> A.f189  axis (0,1,0) through (-83.39,-409.75,140.29)mm
